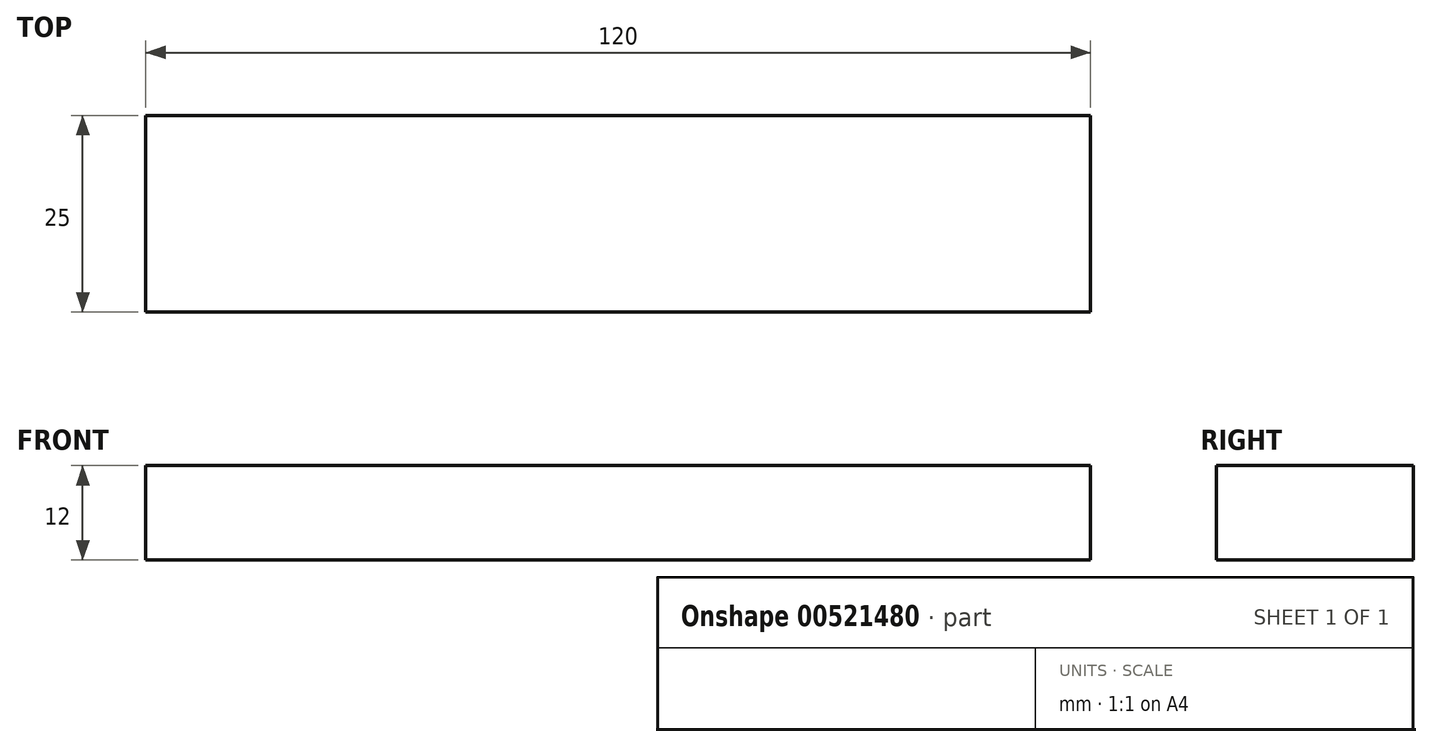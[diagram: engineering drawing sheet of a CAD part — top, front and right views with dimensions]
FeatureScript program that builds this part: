
annotation { "Feature Type Name" : "Feature", "Feature Type Description" : "" }
export const myFeature = defineFeature(function(context is Context, id is Id, definition is map)
    precondition{}
    {
        {
            var Q0;
            Q0=qCreatedBy(makeId("Top.planeOp"),FACE);
            var sketch = newSketch(context, id + "F0", { "sketchPlane" : qUnion([Q0])});
            skLineSegment(sketch, "E0.bottom", {"start": v(-60, 12.5) * mm, "end": v(60, 12.5) * mm});
            skLineSegment(sketch, "E0.top", {"start": v(-60, -12.5) * mm, "end": v(60, -12.5) * mm});
            skLineSegment(sketch, "E0.left", {"start": v(-60, 12.5) * mm, "end": v(-60, -12.5) * mm});
            skLineSegment(sketch, "E0.right", {"start": v(60, 12.5) * mm, "end": v(60, -12.5) * mm});
            skPoint(sketch, "E0.middle", {"position": v(0, 0) * mm});
            skSolve(sketch);
        }
        {
            var Q0;
            Q0=makeQuery(id+"F0.imprint","IMPRINT",FACE,{"disambiguationData":[TD([[makeQuery(id+"F0.imprint","IMPRINT",EDGE,{"derivedFrom":sQuery(id+"F0.wireOp",EDGE,"E0.bottom")}),-1.0]])]});
            extrude(context, id + "F1", {"entities" : qUnion([Q0]), "depth" : 12 * mm, "offsetDistance" : 25 * mm});
        }
    });
